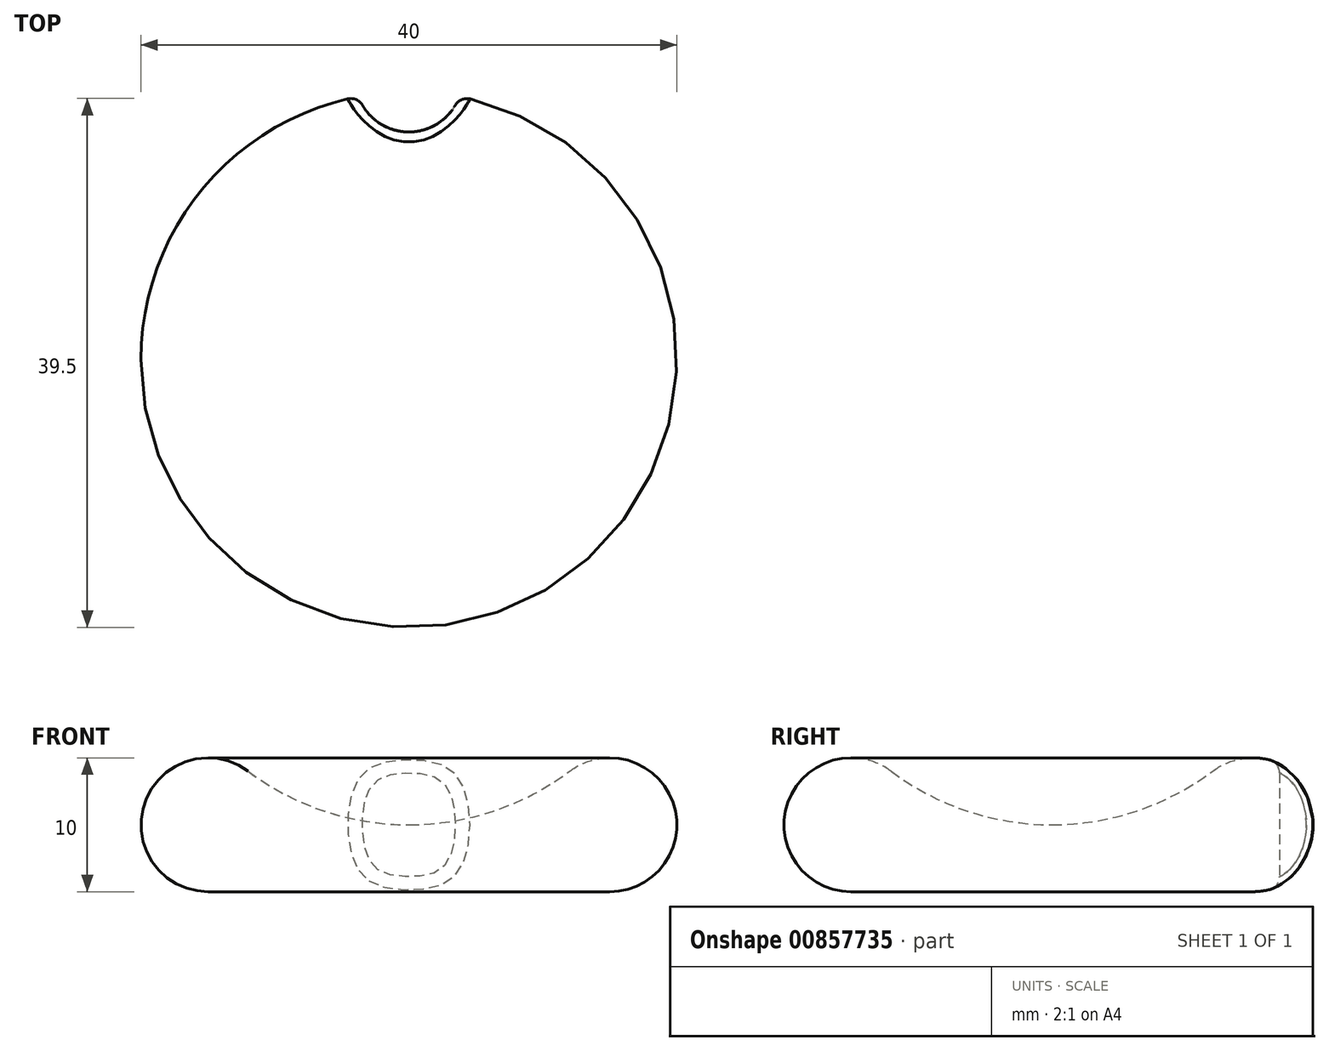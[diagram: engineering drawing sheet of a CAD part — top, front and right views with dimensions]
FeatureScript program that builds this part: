
annotation { "Feature Type Name" : "Feature", "Feature Type Description" : "" }
export const myFeature = defineFeature(function(context is Context, id is Id, definition is map)
    precondition{}
    {
        {
            var Q0;
            Q0=qCreatedBy(makeId("Front.planeOp"),FACE);
            var sketch = newSketch(context, id + "F0", { "sketchPlane" : qUnion([Q0])});
            skArc(sketch, "E0", {"start": v(-12, 9) * mm, "mid": v(-19.74, 6.58) * mm, "end": v(-15, 0) * mm});
            skArc(sketch, "E1", {"start": v(-12, 9) * mm, "mid": v(-6.32, 6.03) * mm, "end": v(0, 5) * mm});
            skLineSegment(sketch, "E2", {"start": v(-15, 0) * mm, "end": v(0, 0) * mm});
            skLineSegment(sketch, "E3", {"start": v(0, 0) * mm, "end": v(0, 5) * mm});
            skSolve(sketch);
        }
        {
            var Q0;
            Q0=makeQuery(id+"F0.imprint","IMPRINT",FACE,{"disambiguationData":[TD([[makeQuery(id+"F0.imprint","IMPRINT",EDGE,{"derivedFrom":sQuery(id+"F0.wireOp",EDGE,"E0")}),1.0]])]});
            var Q1;
            Q1=sQuery(id+"F0.wireOp",EDGE,"E3");
            revolve(context, id + "F1", {"surfaceOperationType" : NewSurfaceOperationType.NEW, "entities" : qUnion([Q0]), "axis" : qUnion([Q1]), "revolveType" : RevolveType.FULL});
        }
        {
            var Q0;
            Q0=qCreatedBy(makeId("Top.planeOp"),FACE);
            var sketch = newSketch(context, id + "F2", { "sketchPlane" : qUnion([Q0])});
            skCircle(sketch, "E4", {"center": v(0, 21) * mm, "radius": 4 * mm});
            skSolve(sketch);
        }
        {
            var Q0;
            Q0 = qSketchRegion(id + "F2", true);
            extrude(context, id + "F3", {"entities" : qUnion([Q0]), "operationType" : NewBodyOperationType.REMOVE, "oppositeDirection" : true, "depth" : 25 * mm, "offsetDistance" : 25 * mm});
        }
        {
            var Q0;
            Q0 = qSketchRegion(id + "F2", true);
            extrude(context, id + "F4", {"entities" : qUnion([Q0]), "operationType" : NewBodyOperationType.REMOVE, "depth" : 13.5 * mm, "offsetDistance" : 25 * mm});
        }
        {
            var Q0;
            Q0=makeQuery(id+"F4.boolean.opBoolean","INTERSECT",EDGE,{"derivedFrom":[makeQuery(id+"F1.opRevolve","SWEPT_FACE",FACE,{"disambiguationData":[OSD([sQuery(id+"F0.wireOp",EDGE,"E0")])]}),makeQuery(id+"F4.opExtrude","SWEPT_FACE",FACE,{"disambiguationData":[OSD([sQuery(id+"F2.wireOp",EDGE,"E4")])]})]});
            fillet(context, id + "F5", {"entities" : qUnion([Q0]), "radius" : 1 * mm, "tangentPropagation" : true, "allowEdgeOverflow" : false});
        }
    });
